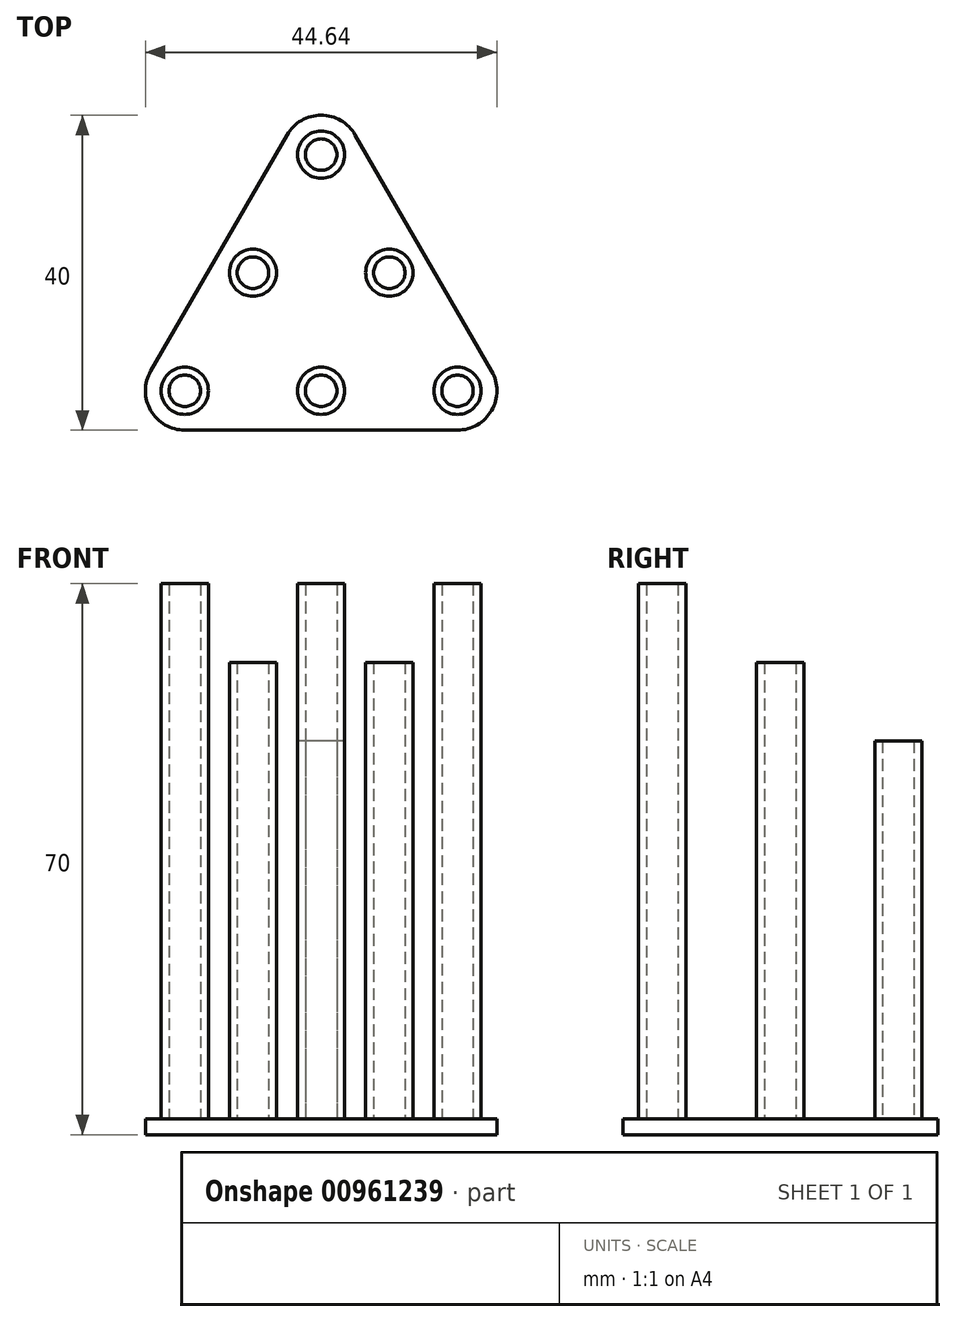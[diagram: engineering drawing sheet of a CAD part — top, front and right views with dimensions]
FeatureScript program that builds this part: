
annotation { "Feature Type Name" : "Feature", "Feature Type Description" : "" }
export const myFeature = defineFeature(function(context is Context, id is Id, definition is map)
    precondition{}
    {
        {
            var Q0;
            Q0=qCreatedBy(makeId("Top.planeOp"),FACE);
            var sketch = newSketch(context, id + "F0", { "sketchPlane" : qUnion([Q0])});
            skLineSegment(sketch, "E0", {"start": v(0, 0) * mm, "end": v(-8.66, -15) * mm, "construction": true});
            skLineSegment(sketch, "E1", {"start": v(-8.66, -15) * mm, "end": v(-17.32, -30) * mm, "construction": true});
            skLineSegment(sketch, "E2", {"start": v(-17.32, -30) * mm, "end": v(0, -30) * mm, "construction": true});
            skLineSegment(sketch, "E3", {"start": v(0, -30) * mm, "end": v(17.32, -30) * mm, "construction": true});
            skLineSegment(sketch, "E4", {"start": v(17.32, -30) * mm, "end": v(8.66, -15) * mm, "construction": true});
            skLineSegment(sketch, "E5", {"start": v(8.66, -15) * mm, "end": v(0, 0) * mm, "construction": true});
            skLineSegment(sketch, "E6", {"start": v(-8.66, -15) * mm, "end": v(0, -30) * mm, "construction": true});
            skLineSegment(sketch, "E7", {"start": v(8.66, -15) * mm, "end": v(0, -30) * mm, "construction": true});
            skCircle(sketch, "E8", {"center": v(0, 0) * mm, "radius": 3 * mm});
            skCircle(sketch, "E9", {"center": v(0, 0) * mm, "radius": 2 * mm});
            skCircle(sketch, "E10", {"center": v(-8.66, -15) * mm, "radius": 2 * mm});
            skCircle(sketch, "E11", {"center": v(-8.66, -15) * mm, "radius": 3 * mm});
            skCircle(sketch, "E12", {"center": v(-17.32, -30) * mm, "radius": 2 * mm});
            skCircle(sketch, "E13", {"center": v(-17.32, -30) * mm, "radius": 3 * mm});
            skCircle(sketch, "E14", {"center": v(0, -30) * mm, "radius": 2 * mm});
            skCircle(sketch, "E15", {"center": v(0, -30) * mm, "radius": 3 * mm});
            skCircle(sketch, "E16", {"center": v(17.32, -30) * mm, "radius": 2 * mm});
            skCircle(sketch, "E17", {"center": v(17.32, -30) * mm, "radius": 3 * mm});
            skCircle(sketch, "E18", {"center": v(8.66, -15) * mm, "radius": 2 * mm});
            skCircle(sketch, "E19", {"center": v(8.66, -15) * mm, "radius": 3 * mm});
            skSolve(sketch);
        }
        {
            var Q0;
            Q0=makeQuery(id+"F0.imprint","IMPRINT",FACE,{"disambiguationData":[TD([[makeQuery(id+"F0.imprint","IMPRINT",EDGE,{"derivedFrom":sQuery(id+"F0.wireOp",EDGE,"E8")}),1.0]])]});
            extrude(context, id + "F1", {"entities" : qUnion([Q0]), "depth" : 50 * mm, "offsetDistance" : 25 * mm});
        }
        {
            var Q0;
            Q0=makeQuery(id+"F0.imprint","IMPRINT",FACE,{"disambiguationData":[TD([[makeQuery(id+"F0.imprint","IMPRINT",EDGE,{"derivedFrom":sQuery(id+"F0.wireOp",EDGE,"E10")}),-1.0]])]});
            extrude(context, id + "F2", {"entities" : qUnion([Q0]), "depth" : 60 * mm, "offsetDistance" : 25 * mm});
        }
        {
            var Q0;
            Q0=makeQuery(id+"F0.imprint","IMPRINT",FACE,{"disambiguationData":[TD([[makeQuery(id+"F0.imprint","IMPRINT",EDGE,{"derivedFrom":sQuery(id+"F0.wireOp",EDGE,"E18")}),-1.0]])]});
            extrude(context, id + "F3", {"entities" : qUnion([Q0]), "depth" : 60 * mm, "offsetDistance" : 25 * mm});
        }
        {
            var Q0;
            Q0=makeQuery(id+"F0.imprint","IMPRINT",FACE,{"disambiguationData":[TD([[makeQuery(id+"F0.imprint","IMPRINT",EDGE,{"derivedFrom":sQuery(id+"F0.wireOp",EDGE,"E16")}),-1.0]])]});
            extrude(context, id + "F4", {"entities" : qUnion([Q0]), "depth" : 70 * mm, "offsetDistance" : 25 * mm});
        }
        {
            var Q0;
            Q0=makeQuery(id+"F0.imprint","IMPRINT",FACE,{"disambiguationData":[TD([[makeQuery(id+"F0.imprint","IMPRINT",EDGE,{"derivedFrom":sQuery(id+"F0.wireOp",EDGE,"E14")}),-1.0]])]});
            extrude(context, id + "F5", {"entities" : qUnion([Q0]), "depth" : 70 * mm, "offsetDistance" : 25 * mm});
        }
        {
            var Q0;
            Q0=makeQuery(id+"F0.imprint","IMPRINT",FACE,{"disambiguationData":[TD([[makeQuery(id+"F0.imprint","IMPRINT",EDGE,{"derivedFrom":sQuery(id+"F0.wireOp",EDGE,"E12")}),-1.0]])]});
            extrude(context, id + "F6", {"entities" : qUnion([Q0]), "depth" : 70 * mm, "offsetDistance" : 25 * mm});
        }
        {
            var Q0;
            Q0=qCreatedBy(makeId("Top.planeOp"),FACE);
            var sketch = newSketch(context, id + "F7", { "sketchPlane" : qUnion([Q0])});
            skLineSegment(sketch, "E20", {"start": v(-25.98, -35) * mm, "end": v(0, 10) * mm});
            skLineSegment(sketch, "E21", {"start": v(0, 10) * mm, "end": v(25.98, -35) * mm});
            skLineSegment(sketch, "E22", {"start": v(25.98, -35) * mm, "end": v(-25.98, -35) * mm});
            skSolve(sketch);
        }
        {
            var Q0;
            Q0 = qSketchRegion(id + "F7", true);
            extrude(context, id + "F8", {"entities" : qUnion([Q0]), "operationType" : NewBodyOperationType.ADD, "depth" : 2 * mm, "offsetDistance" : 25 * mm});
        }
        {
            var Q0;
            Q0=makeQuery(id+"F8.opExtrude","SWEPT_EDGE",EDGE,{"disambiguationData":[OSD([sQuery(id+"F7.wireOp",EDGE,"E20"),sQuery(id+"F7.wireOp",EDGE,"E21")])]});
            var Q1;
            Q1=makeQuery(id+"F8.opExtrude","SWEPT_EDGE",EDGE,{"disambiguationData":[OSD([sQuery(id+"F7.wireOp",EDGE,"E20"),sQuery(id+"F7.wireOp",EDGE,"E22")])]});
            var Q2;
            Q2=makeQuery(id+"F8.opExtrude","SWEPT_EDGE",EDGE,{"disambiguationData":[OSD([sQuery(id+"F7.wireOp",EDGE,"E21"),sQuery(id+"F7.wireOp",EDGE,"E22")])]});
            fillet(context, id + "F9", {"entities" : qUnion([Q0, Q1, Q2]), "radius" : 5 * mm, "tangentPropagation" : true, "allowEdgeOverflow" : false});
        }
    });
